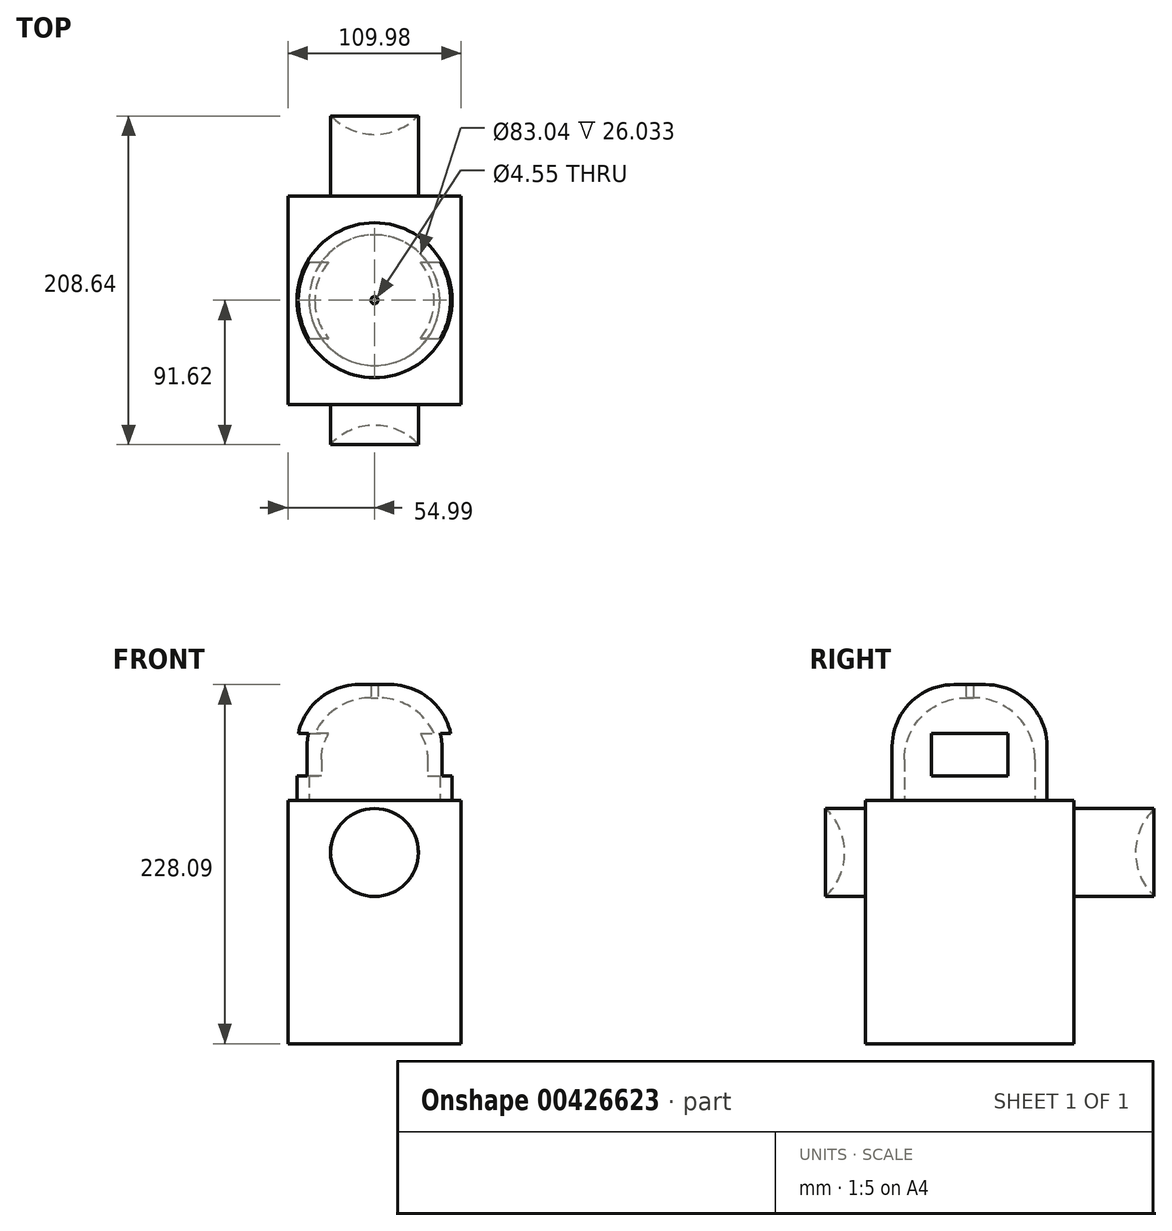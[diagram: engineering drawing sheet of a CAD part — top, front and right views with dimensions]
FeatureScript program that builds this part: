
annotation { "Feature Type Name" : "Feature", "Feature Type Description" : "" }
export const myFeature = defineFeature(function(context is Context, id is Id, definition is map)
    precondition{}
    {
        {
            var Q0;
            Q0=qCreatedBy(makeId("Top.planeOp"),FACE);
            var sketch = newSketch(context, id + "F0", { "sketchPlane" : qUnion([Q0])});
            skCircle(sketch, "E0", {"center": v(0, 0) * mm, "radius": 49.21 * mm});
            skSolve(sketch);
        }
        {
            var Q0;
            Q0 = qSketchRegion(id + "F0", true);
            extrude(context, id + "F1", {"entities" : qUnion([Q0]), "depth" : 73.66 * mm});
        }
        {
            var Q0;
            Q0=qCreatedBy(makeId("Right.planeOp"),FACE);
            var sketch = newSketch(context, id + "F2", { "sketchPlane" : qUnion([Q0])});
            skLineSegment(sketch, "E1.bottom", {"start": v(24.23, 42.5) * mm, "end": v(-24.23, 42.5) * mm});
            skLineSegment(sketch, "E1.top", {"start": v(24.23, 15.67) * mm, "end": v(-24.23, 15.67) * mm});
            skLineSegment(sketch, "E1.left", {"start": v(24.23, 42.5) * mm, "end": v(24.23, 15.67) * mm});
            skLineSegment(sketch, "E1.right", {"start": v(-24.23, 42.5) * mm, "end": v(-24.23, 15.67) * mm});
            skPoint(sketch, "E1.middle", {"position": v(0, 29.08) * mm});
            skSolve(sketch);
        }
        {
            var Q0;
            Q0 = qSketchRegion(id + "F2", true);
            extrude(context, id + "F3", {"entities" : qUnion([Q0]), "operationType" : NewBodyOperationType.REMOVE, "endBound" : BoundingType.SYMMETRIC, "oppositeDirection" : true, "depth" : 147.32 * mm});
        }
        {
            var Q0;
            Q0=makeQuery(id+"F1.opExtrude","CAP_FACE",FACE,{"disambiguationData":[OSD([sQuery(id+"F0.wireOp",EDGE,"E0")])],"isStart":true});
            var sketch = newSketch(context, id + "F4", { "sketchPlane" : qUnion([Q0])});
            skCircle(sketch, "E2", {"center": v(0, 0) * mm, "radius": 41.52 * mm});
            skSolve(sketch);
        }
        {
            var Q0;
            Q0 = qSketchRegion(id + "F4", true);
            extrude(context, id + "F5", {"entities" : qUnion([Q0]), "operationType" : NewBodyOperationType.REMOVE, "oppositeDirection" : true, "depth" : 65.28 * mm});
        }
        {
            var Q0;
            Q0=makeQuery(id+"F1.opExtrude","CAP_EDGE",EDGE,{"disambiguationData":[OSD([sQuery(id+"F0.wireOp",EDGE,"E0")])],"isStart":false});
            var Q1;
            Q1=makeQuery(id+"F5.boolean.opBoolean","COPY",EDGE,{"derivedFrom":makeQuery(id+"F5.opExtrude","CAP_EDGE",EDGE,{"disambiguationData":[OSD([sQuery(id+"F4.wireOp",EDGE,"E2")])],"isStart":false})});
            fillet(context, id + "F6", {"entities" : qUnion([Q0, Q1]), "radius" : 39.25 * mm, "tangentPropagation" : true, "allowEdgeOverflow" : false});
        }
        {
            var Q0;
            Q0=makeQuery(id+"F5.boolean.opBoolean","COPY",FACE,{"derivedFrom":makeQuery(id+"F5.opExtrude","CAP_FACE",FACE,{"disambiguationData":[OSD([sQuery(id+"F4.wireOp",EDGE,"E2")])],"isStart":false})});
            extrude(context, id + "F7", {"entities" : qUnion([Q0]), "operationType" : NewBodyOperationType.REMOVE, "oppositeDirection" : true, "depth" : 25.4 * mm});
        }
        {
            var Q0;
            Q0=makeQuery(id+"F1.opExtrude","CAP_FACE",FACE,{"disambiguationData":[OSD([sQuery(id+"F0.wireOp",EDGE,"E0")])],"isStart":true});
            var sketch = newSketch(context, id + "F8", { "sketchPlane" : qUnion([Q0])});
            skLineSegment(sketch, "E3.bottom", {"start": v(55, 66.22) * mm, "end": v(-55, 66.22) * mm});
            skLineSegment(sketch, "E3.top", {"start": v(55, -66.22) * mm, "end": v(-55, -66.22) * mm});
            skLineSegment(sketch, "E3.left", {"start": v(55, 66.22) * mm, "end": v(55, -66.22) * mm});
            skLineSegment(sketch, "E3.right", {"start": v(-55, 66.22) * mm, "end": v(-55, -66.22) * mm});
            skPoint(sketch, "E3.middle", {"position": v(0, 0) * mm});
            skSolve(sketch);
        }
        {
            var Q0;
            Q0 = qSketchRegion(id + "F8", true);
            extrude(context, id + "F9", {"entities" : qUnion([Q0]), "depth" : 154.43 * mm});
        }
        {
            var Q0;
            Q0=makeQuery(id+"F9.opExtrude","SWEPT_FACE",FACE,{"disambiguationData":[OSD([sQuery(id+"F8.wireOp",EDGE,"E3.top")])]});
            var sketch = newSketch(context, id + "F10", { "sketchPlane" : qUnion([Q0])});
            skCircle(sketch, "E4", {"center": v(0, -33.02) * mm, "radius": 27.94 * mm});
            skSolve(sketch);
        }
        {
            var Q0;
            Q0 = qSketchRegion(id + "F10", true);
            extrude(context, id + "F11", {"entities" : qUnion([Q0]), "depth" : 25.4 * mm});
        }
        {
            var Q0;
            Q0=makeQuery(id+"F11.opExtrude","CAP_FACE",FACE,{"disambiguationData":[OSD([sQuery(id+"F10.wireOp",EDGE,"E4")])],"isStart":false});
            var sketch = newSketch(context, id + "F12", { "sketchPlane" : qUnion([Q0])});
            skCircle(sketch, "E5", {"center": v(0, -33.02) * mm, "radius": 27.94 * mm});
            skSolve(sketch);
        }
        {
            var Q0;
            Q0=makeQuery(id+"F11.opExtrude","CAP_FACE",FACE,{"disambiguationData":[OSD([sQuery(id+"F10.wireOp",EDGE,"E4")])],"isStart":false});
            var sketch = newSketch(context, id + "F13", { "sketchPlane" : qUnion([Q0])});
            skCircle(sketch, "E6", {"center": v(0, -33.02) * mm, "radius": 27.94 * mm});
            skLineSegment(sketch, "E7", {"start": v(0, -5.08) * mm, "end": v(0, -60.96) * mm});
            skSolve(sketch);
        }
        {
            var Q0;
            Q0=qCreatedBy(makeId("Right.planeOp"),FACE);
            var sketch = newSketch(context, id + "F14", { "sketchPlane" : qUnion([Q0])});
            skArc(sketch, "E8", {"start": v(91.62, -5.08) * mm, "mid": v(79.43, -33.02) * mm, "end": v(91.62, -60.96) * mm});
            skLineSegment(sketch, "E9", {"start": v(91.62, -5.08) * mm, "end": v(91.62, -60.96) * mm});
            skPoint(sketch, "E10.orphan", {"position": v(117.53, 5.08) * mm});
            skLineSegment(sketch, "E11", {"start": v(117.53, -33.02) * mm, "end": v(117.53, -20.32) * mm});
            skLineSegment(sketch, "E12", {"start": v(91.62, -33.02) * mm, "end": v(79.43, -33.02) * mm});
            skSolve(sketch);
        }
        {
            var Q0;
            Q0 = qSketchRegion(id + "F14", true);
            var Q1;
            Q1=sQuery(id+"F14.wireOp",EDGE,"E11");
            revolve(context, id + "F15", {"operationType" : NewBodyOperationType.REMOVE, "entities" : qUnion([Q0]), "axis" : qUnion([Q1]), "revolveType" : RevolveType.FULL, "oppositeDirection" : true});
        }
        {
            var Q0;
            Q0=makeQuery(id+"F11.opExtrude","SWEPT_BODY",BODY,{"disambiguationData":[OSD([sQuery(id+"F10.wireOp",EDGE,"E4")])]});
            var Q1;
            Q1=qCreatedBy(makeId("Front.planeOp"),FACE);
            mirror(context, id + "F16", {"operationType" : NewBodyOperationType.ADD, "entities" : qUnion([Q0]), "mirrorPlane" : qUnion([Q1])});
        }
        {
            var Q0;
            Q0 = qSketchRegion(id + "F12", true);
            extrude(context, id + "F17", {"entities" : qUnion([Q0]), "depth" : 25.4 * mm});
        }
        {
            var Q0;
            {var subQ3=sQuery(id+"F14.wireOp",EDGE,"E12");Q0=makeQuery(id+"F14.imprint","IMPRINT",FACE,{"disambiguationData":[TD([[makeQuery(id+"F14.imprint","IMPRINT",EDGE,{"derivedFrom":subQ3}),-1.0]])]});}
            var Q1;
            Q1=sQuery(id+"F14.wireOp",EDGE,"E12");
            revolve(context, id + "F18", {"operationType" : NewBodyOperationType.ADD, "entities" : qUnion([Q0]), "axis" : qUnion([Q1]), "revolveType" : RevolveType.FULL});
        }
        {
            var Q0;
            Q0=qCreatedBy(makeId("Right.planeOp"),FACE);
            var sketch = newSketch(context, id + "F19", { "sketchPlane" : qUnion([Q0])});
            skArc(sketch, "E13", {"start": v(117.53, -5.08) * mm, "mid": v(105.33, -33.02) * mm, "end": v(117.53, -60.96) * mm});
            skLineSegment(sketch, "E14", {"start": v(117.53, -5.08) * mm, "end": v(117.53, -60.96) * mm});
            skLineSegment(sketch, "E15", {"start": v(143.43, -20.32) * mm, "end": v(143.43, -33.02) * mm});
            skSolve(sketch);
        }
        {
            var Q0;
            Q0 = qSketchRegion(id + "F19", true);
            var Q1;
            Q1=sQuery(id+"F19.wireOp",EDGE,"E15");
            revolve(context, id + "F20", {"operationType" : NewBodyOperationType.REMOVE, "entities" : qUnion([Q0]), "axis" : qUnion([Q1]), "revolveType" : RevolveType.FULL, "oppositeDirection" : true});
        }
    });
